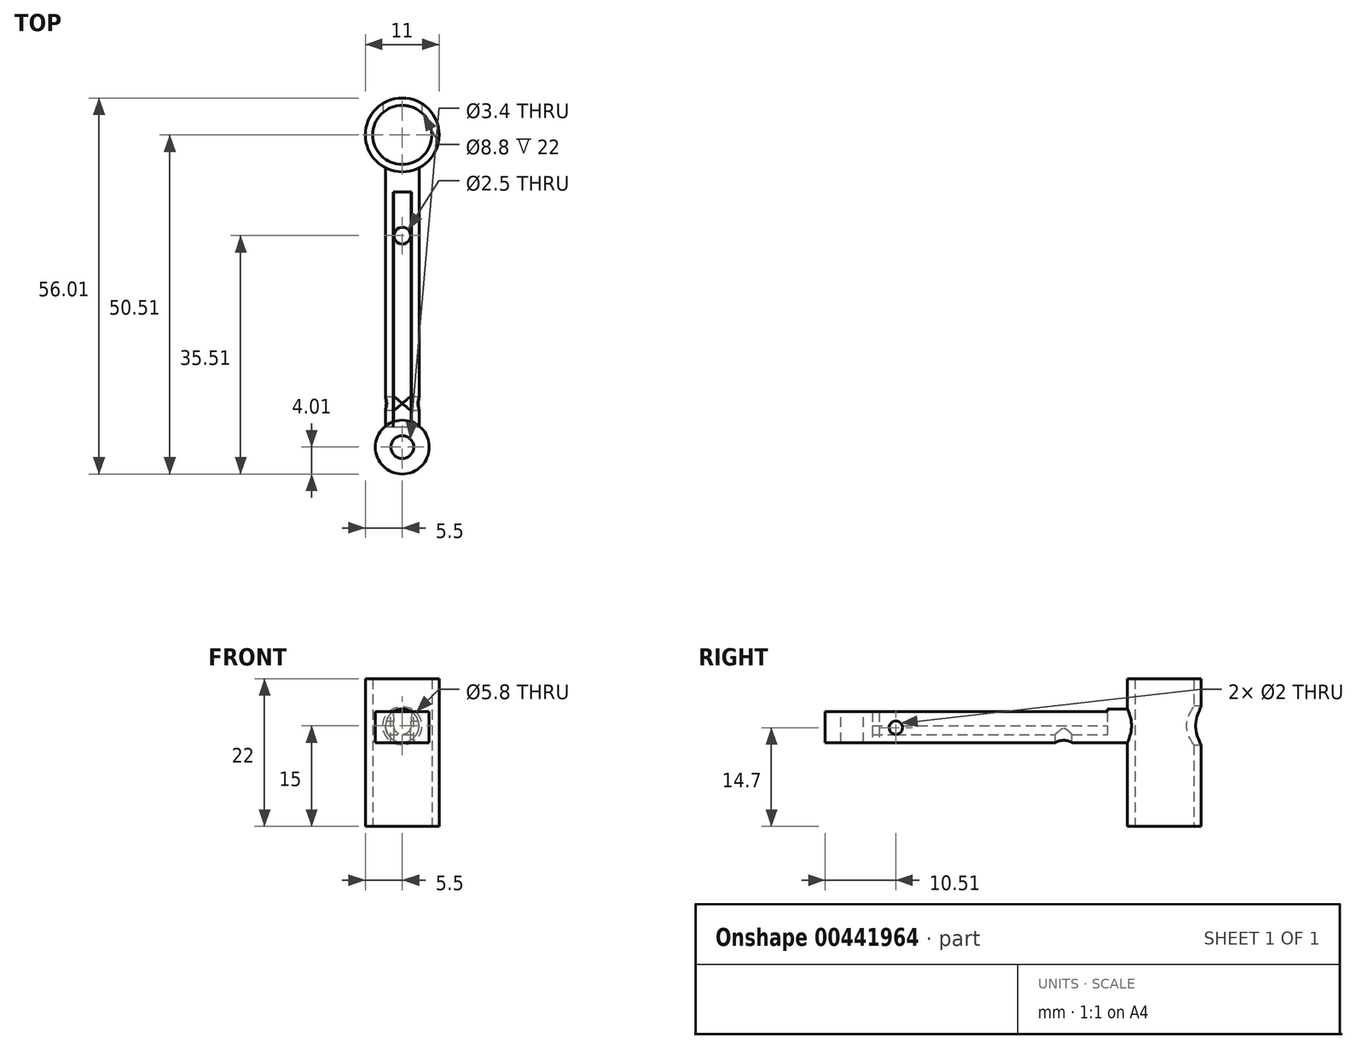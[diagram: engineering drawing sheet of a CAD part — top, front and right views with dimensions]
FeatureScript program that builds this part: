
annotation { "Feature Type Name" : "Feature", "Feature Type Description" : "" }
export const myFeature = defineFeature(function(context is Context, id is Id, definition is map)
    precondition{}
    {
        {
            var Q0;
            Q0=qCreatedBy(makeId("Top.planeOp"),FACE);
            var sketch = newSketch(context, id + "F0", { "sketchPlane" : qUnion([Q0])});
            skCircle(sketch, "E0", {"center": v(0, 0) * mm, "radius": 4.4 * mm});
            skCircle(sketch, "E1", {"center": v(0, 0) * mm, "radius": 5.5 * mm});
            skCircle(sketch, "E2", {"center": v(0, 0) * mm, "radius": 2.54 * mm});
            skPoint(sketch, "E3", {"position": v(-3, 3.22) * mm});
            skPoint(sketch, "E4", {"position": v(3, 3.22) * mm});
            skPoint(sketch, "E5", {"position": v(-3, 4.6) * mm});
            skPoint(sketch, "E6", {"position": v(3, 4.6) * mm});
            skLineSegment(sketch, "E7", {"start": v(-3, 3.22) * mm, "end": v(-3, 4.6) * mm});
            skLineSegment(sketch, "E8", {"start": v(3, 3.22) * mm, "end": v(3, 4.6) * mm});
            skPoint(sketch, "E9", {"position": v(-2.54, 0) * mm});
            skPoint(sketch, "E10", {"position": v(2.54, 0) * mm});
            skCircle(sketch, "E11", {"center": v(-2.54, 0) * mm, "radius": 1.25 * mm});
            skCircle(sketch, "E12", {"center": v(2.54, 0) * mm, "radius": 1.25 * mm});
            skSolve(sketch);
        }
        {
            var Q0;
            Q0=qSketchRegion(id+"F0",true);
            extrude(context, id + "F1", {"entities" : qUnion([Q0]), "depth" : 22 * mm, "offsetDistance" : 25.4 * mm});
        }
        {
            var Q0;
            Q0=makeQuery(id+"F0.imprint","IMPRINT",FACE,{"disambiguationData":[TD([[makeQuery(id+"F0.imprint","IMPRINT",EDGE,{"derivedFrom":sQuery(id+"F0.wireOp",EDGE,"E0")}),1.0]])]});
            extrude(context, id + "F2", {"entities" : qUnion([Q0]), "operationType" : NewBodyOperationType.ADD, "depth" : 2 * mm, "offsetDistance" : 25.4 * mm});
        }
        {
            var Q0;
            Q0=qCreatedBy(makeId("Front.planeOp"),FACE);
            var sketch = newSketch(context, id + "F3", { "sketchPlane" : qUnion([Q0])});
            skPoint(sketch, "E13", {"position": v(0, 15) * mm});
            skCircle(sketch, "E14", {"center": v(0, 15) * mm, "radius": 2 * mm});
            skSolve(sketch);
        }
        {
            var Q0;
            Q0=sQuery(id+"F3.wireOp",VERTEX,"E13");
            var Q1;
            Q1=makeQuery(id+"F1.opExtrude","SWEPT_BODY",BODY,{"disambiguationData":[OSD([sQuery(id+"F0.wireOp",EDGE,"E0"),sQuery(id+"F0.wireOp",EDGE,"E1")])]});
            hole(context, id + "F4", {"style" : HoleStyle.SIMPLE, "endStyle" : HoleEndStyle.THROUGH, "holeDiameter" : 5.8 * mm, "majorDiameter" : 6.35 * mm, "isTappedThrough" : true, "tappedDepth" : 12.7 * mm, "tapClearance" : 3, "locations" : qUnion([Q0]), "scope" : qUnion([Q1])});
        }
        {
            var Q0;
            Q0=qCreatedBy(makeId("Front.planeOp"),FACE);
            var sketch = newSketch(context, id + "F5", { "sketchPlane" : qUnion([Q0])});
            skCircle(sketch, "E15", {"center": v(0, 15) * mm, "radius": 2.5 * mm});
            skPoint(sketch, "E16", {"position": v(-1.73, 16.8) * mm});
            skPoint(sketch, "E17", {"position": v(1.73, 16.8) * mm});
            skLineSegment(sketch, "E18", {"start": v(-1.73, 16.8) * mm, "end": v(1.73, 16.8) * mm});
            skSolve(sketch);
        }
        {
            var Q0;
            Q0=qSketchRegion(id+"F5",true);
            extrude(context, id + "F6", {"entities" : qUnion([Q0]), "operationType" : NewBodyOperationType.ADD, "depth" : 8.48 * mm, "offsetDistance" : 25.4 * mm});
        }
        {
            var Q0;
            Q0=makeQuery(id+"F6.opExtrude","CAP_FACE",FACE,{"disambiguationData":[OSD([sQuery(id+"F5.wireOp",EDGE,"E15")])],"isStart":false});
            var sketch = newSketch(context, id + "F7", { "sketchPlane" : qUnion([Q0])});
            skPoint(sketch, "E19", {"position": v(-1.36, 17.1) * mm});
            skPoint(sketch, "E20", {"position": v(1.36, 17.1) * mm});
            skCircle(sketch, "E21", {"center": v(0, 15) * mm, "radius": 1.3 * mm});
            skPoint(sketch, "E22", {"position": v(-1.3, 15) * mm});
            skPoint(sketch, "E23", {"position": v(1.3, 15) * mm});
            skLineSegment(sketch, "E24", {"start": v(-1.36, 17.1) * mm, "end": v(-1.3, 15) * mm});
            skLineSegment(sketch, "E25", {"start": v(1.36, 17.1) * mm, "end": v(1.3, 15) * mm});
            skSolve(sketch);
        }
        {
            var Q0;
            {var subQ0=sQuery(id+"F7.wireOp",EDGE,"E24");Q0=makeQuery(id+"F7.imprint","IMPRINT",FACE,{"disambiguationData":[TD([[makeQuery(id+"F7.imprint","IMPRINT",EDGE,{"derivedFrom":subQ0}),-1.0]])]});}
            extrude(context, id + "F8", {"entities" : qUnion([Q0]), "operationType" : NewBodyOperationType.ADD, "depth" : 35 * mm, "offsetDistance" : 25.4 * mm});
        }
        {
            var Q0;
            Q0=makeQuery(id+"F1.opExtrude","CAP_FACE",FACE,{"disambiguationData":[OSD([sQuery(id+"F0.wireOp",EDGE,"E0"),sQuery(id+"F0.wireOp",EDGE,"E1")])],"isStart":false});
            var sketch = newSketch(context, id + "F9", { "sketchPlane" : qUnion([Q0])});
            skPoint(sketch, "E26", {"position": v(0, 0) * mm});
            skPoint(sketch, "E27", {"position": v(0, -15) * mm});
            skCircle(sketch, "E28", {"center": v(0, -15) * mm, "radius": 1.25 * mm});
            skSolve(sketch);
        }
        {
            var Q0;
            Q0=makeQuery(id+"F9.imprint","IMPRINT",FACE,{"disambiguationData":[TD([[makeQuery(id+"F9.imprint","IMPRINT",EDGE,{"derivedFrom":sQuery(id+"F9.wireOp",EDGE,"E28")}),1.0]])]});
            extrude(context, id + "F10", {"entities" : qUnion([Q0]), "operationType" : NewBodyOperationType.REMOVE, "oppositeDirection" : true, "depth" : 25.4 * mm, "offsetDistance" : 25.4 * mm});
        }
        {
            var Q0;
            Q0=makeQuery(id+"F1.opExtrude","CAP_FACE",FACE,{"disambiguationData":[OSD([sQuery(id+"F0.wireOp",EDGE,"E1"),sQuery(id+"F0.wireOp",EDGE,"E0")])],"isStart":false});
            var sketch = newSketch(context, id + "F11", { "sketchPlane" : qUnion([Q0])});
            skCircle(sketch, "E29", {"center": v(0, 0) * mm, "radius": 4.4 * mm});
            skSolve(sketch);
        }
        {
            var Q0;
            Q0 = qSketchRegion(id + "F11", true);
            extrude(context, id + "F12", {"entities" : qUnion([Q0]), "operationType" : NewBodyOperationType.REMOVE, "oppositeDirection" : true, "depth" : 25.4 * mm, "offsetDistance" : 25.4 * mm});
        }
        {
            var Q0;
            Q0=qCreatedBy(makeId("Right.planeOp"),FACE);
            var sketch = newSketch(context, id + "F13", { "sketchPlane" : qUnion([Q0])});
            skPoint(sketch, "E30", {"position": v(-42.5, 0) * mm});
            skLineSegment(sketch, "E31", {"start": v(-42.5, 0) * mm, "end": v(-42.5, 14.8) * mm});
            skPoint(sketch, "E32", {"position": v(-46.5, 14.8) * mm});
            skPoint(sketch, "E33", {"position": v(-42.5, 17.1) * mm});
            skPoint(sketch, "E34", {"position": v(-42.5, 12.5) * mm});
            skLineSegment(sketch, "E35", {"start": v(-42.5, 17.1) * mm, "end": v(-42.5, 12.5) * mm});
            skPoint(sketch, "E36", {"position": v(-42.5, 14.8) * mm});
            skLineSegment(sketch, "E37", {"start": v(-46.5, 14.8) * mm, "end": v(-46.5, 17.1) * mm});
            skLineSegment(sketch, "E38", {"start": v(-46.5, 17.1) * mm, "end": v(-46.5, 12.5) * mm});
            skLineSegment(sketch, "E39.bottom", {"start": v(-46.5, 12.5) * mm, "end": v(-42.5, 12.5) * mm});
            skLineSegment(sketch, "E39.top", {"start": v(-46.5, 17.1) * mm, "end": v(-42.5, 17.1) * mm});
            skLineSegment(sketch, "E39.left", {"start": v(-46.5, 12.5) * mm, "end": v(-46.5, 17.1) * mm});
            skLineSegment(sketch, "E39.right", {"start": v(-42.5, 12.5) * mm, "end": v(-42.5, 17.1) * mm});
            skSolve(sketch);
        }
        {
            var Q0;
            {var subQ4=sQuery(id+"F13.wireOp",EDGE,"E39.top");Q0=makeQuery(id+"F13.imprint","IMPRINT",FACE,{"disambiguationData":[TD([[makeQuery(id+"F13.imprint","IMPRINT",EDGE,{"derivedFrom":subQ4}),-1.0]])]});}
            var Q1;
            Q1=sQuery(id+"F13.wireOp",EDGE,"E39.left");
            revolve(context, id + "F14", {"entities" : qUnion([Q0]), "axis" : qUnion([Q1]), "revolveType" : RevolveType.FULL});
        }
        {
            var Q0;
            Q0=makeQuery(id+"F14.opRevolve","SWEPT_FACE",FACE,{"disambiguationData":[OSD([sQuery(id+"F13.wireOp",EDGE,"E39.top")])]});
            var sketch = newSketch(context, id + "F15", { "sketchPlane" : qUnion([Q0])});
            skCircle(sketch, "E40", {"center": v(0, -46.5) * mm, "radius": 1.7 * mm});
            skSolve(sketch);
        }
        {
            var Q0;
            Q0=makeQuery(id+"F15.imprint","IMPRINT",FACE,{"disambiguationData":[TD([[makeQuery(id+"F15.imprint","IMPRINT",EDGE,{"derivedFrom":sQuery(id+"F15.wireOp",EDGE,"E40")}),1.0]])]});
            extrude(context, id + "F16", {"entities" : qUnion([Q0]), "operationType" : NewBodyOperationType.REMOVE, "oppositeDirection" : true, "depth" : 25.4 * mm, "offsetDistance" : 25.4 * mm});
        }
        {
            var Q0;
            Q0=qCreatedBy(makeId("Right.planeOp"),FACE);
            var sketch = newSketch(context, id + "F17", { "sketchPlane" : qUnion([Q0])});
            skLineSegment(sketch, "E41", {"start": v(0, 0) * mm, "end": v(-40, 0) * mm});
            skLineSegment(sketch, "E42", {"start": v(-40, 0) * mm, "end": v(-40, 14.7) * mm});
            skCircle(sketch, "E43", {"center": v(-40, 14.7) * mm, "radius": 1 * mm});
            skSolve(sketch);
        }
        {
            var Q0;
            Q0 = qSketchRegion(id + "F17", true);
            extrude(context, id + "F18", {"entities" : qUnion([Q0]), "operationType" : NewBodyOperationType.REMOVE, "endBound" : BoundingType.SYMMETRIC, "oppositeDirection" : true, "depth" : 10 * mm, "offsetDistance" : 25.4 * mm});
        }
    });
